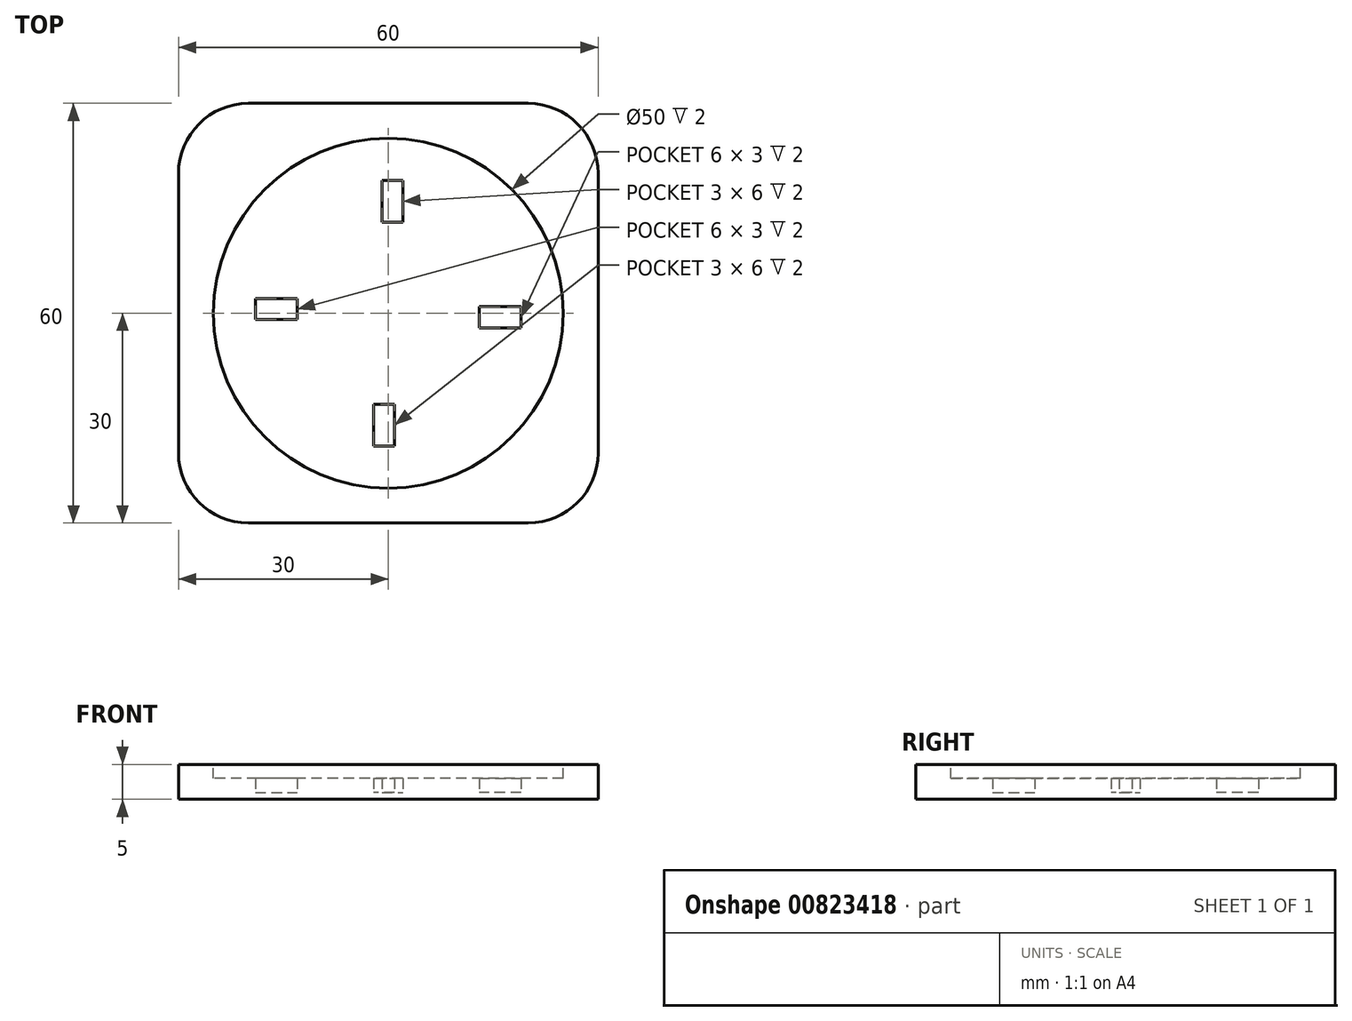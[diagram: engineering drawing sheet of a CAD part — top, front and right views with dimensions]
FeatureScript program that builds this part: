
annotation { "Feature Type Name" : "Feature", "Feature Type Description" : "" }
export const myFeature = defineFeature(function(context is Context, id is Id, definition is map)
    precondition{}
    {
        {
            var Q0;
            Q0=qCreatedBy(makeId("Top.planeOp"),FACE);
            var sketch = newSketch(context, id + "F0", { "sketchPlane" : qUnion([Q0])});
            skLineSegment(sketch, "E0.bottom", {"start": v(30, 30) * mm, "end": v(-30, 30) * mm});
            skLineSegment(sketch, "E0.top", {"start": v(30, -30) * mm, "end": v(-30, -30) * mm});
            skLineSegment(sketch, "E0.left", {"start": v(30, 30) * mm, "end": v(30, -30) * mm});
            skLineSegment(sketch, "E0.right", {"start": v(-30, 30) * mm, "end": v(-30, -30) * mm});
            skPoint(sketch, "E0.middle", {"position": v(0, 0) * mm});
            skSolve(sketch);
        }
        {
            var Q0;
            Q0 = qSketchRegion(id + "F0", true);
            extrude(context, id + "F1", {"entities" : qUnion([Q0]), "depth" : 5 * mm, "offsetDistance" : 25 * mm});
        }
        {
            var Q0;
            Q0=makeQuery(id+"F1.opExtrude","CAP_FACE",FACE,{"disambiguationData":[OSD([sQuery(id+"F0.wireOp",EDGE,"E0.bottom"),sQuery(id+"F0.wireOp",EDGE,"E0.top"),sQuery(id+"F0.wireOp",EDGE,"E0.left"),sQuery(id+"F0.wireOp",EDGE,"E0.right")])],"isStart":false});
            var sketch = newSketch(context, id + "F2", { "sketchPlane" : qUnion([Q0])});
            skCircle(sketch, "E1", {"center": v(0, 0) * mm, "radius": 25 * mm});
            skSolve(sketch);
        }
        {
            var Q0;
            Q0 = qSketchRegion(id + "F2", true);
            extrude(context, id + "F3", {"entities" : qUnion([Q0]), "operationType" : NewBodyOperationType.REMOVE, "oppositeDirection" : true, "depth" : 2 * mm, "offsetDistance" : 25 * mm});
        }
        {
            var Q0;
            Q0=makeQuery(id+"F3.boolean.opBoolean","COPY",FACE,{"derivedFrom":makeQuery(id+"F3.opExtrude","CAP_FACE",FACE,{"disambiguationData":[OSD([sQuery(id+"F2.wireOp",EDGE,"E1")])],"isStart":false})});
            var sketch = newSketch(context, id + "F4", { "sketchPlane" : qUnion([Q0])});
            skLineSegment(sketch, "E2.bottom", {"start": v(-0.91, 19) * mm, "end": v(2.09, 19) * mm});
            skLineSegment(sketch, "E2.top", {"start": v(-0.91, 13) * mm, "end": v(2.09, 13) * mm});
            skLineSegment(sketch, "E2.left", {"start": v(-0.91, 19) * mm, "end": v(-0.91, 13) * mm});
            skLineSegment(sketch, "E2.right", {"start": v(2.09, 19) * mm, "end": v(2.09, 13) * mm});
            skPoint(sketch, "E3.left.start.orphan", {"position": v(8.09, 0) * mm});
            skLineSegment(sketch, "E4.1.0", {"start": v(-19, 2.09) * mm, "end": v(-13, 2.09) * mm});
            skLineSegment(sketch, "E4.1.1", {"start": v(-19, -0.91) * mm, "end": v(-13, -0.91) * mm});
            skLineSegment(sketch, "E4.1.2", {"start": v(-19, -0.91) * mm, "end": v(-19, 2.09) * mm});
            skLineSegment(sketch, "E4.1.3", {"start": v(-13, -0.91) * mm, "end": v(-13, 2.09) * mm});
            skLineSegment(sketch, "E4.2.0", {"start": v(-2.09, -19) * mm, "end": v(-2.09, -13) * mm});
            skLineSegment(sketch, "E4.2.1", {"start": v(0.91, -19) * mm, "end": v(0.91, -13) * mm});
            skLineSegment(sketch, "E4.2.2", {"start": v(0.91, -19) * mm, "end": v(-2.09, -19) * mm});
            skLineSegment(sketch, "E4.2.3", {"start": v(0.91, -13) * mm, "end": v(-2.09, -13) * mm});
            skLineSegment(sketch, "E4.3.0", {"start": v(19, -2.09) * mm, "end": v(13, -2.09) * mm});
            skLineSegment(sketch, "E4.3.1", {"start": v(19, 0.91) * mm, "end": v(13, 0.91) * mm});
            skLineSegment(sketch, "E4.3.2", {"start": v(19, 0.91) * mm, "end": v(19, -2.09) * mm});
            skLineSegment(sketch, "E4.3.3", {"start": v(13, 0.91) * mm, "end": v(13, -2.09) * mm});
            skPoint(sketch, "E4.center", {"position": v(0, 0) * mm});
            skSolve(sketch);
        }
        {
            var Q0;
            Q0=makeQuery(id+"F4.imprint","IMPRINT",FACE,{"disambiguationData":[TD([[makeQuery(id+"F4.imprint","IMPRINT",EDGE,{"derivedFrom":sQuery(id+"F4.wireOp",EDGE,"E4.2.0")}),-1.0]])]});
            var Q1;
            Q1=makeQuery(id+"F4.imprint","IMPRINT",FACE,{"disambiguationData":[TD([[makeQuery(id+"F4.imprint","IMPRINT",EDGE,{"derivedFrom":sQuery(id+"F4.wireOp",EDGE,"E4.1.0")}),-1.0]])]});
            var Q2;
            Q2=makeQuery(id+"F4.imprint","IMPRINT",FACE,{"disambiguationData":[TD([[makeQuery(id+"F4.imprint","IMPRINT",EDGE,{"derivedFrom":sQuery(id+"F4.wireOp",EDGE,"E2.bottom")}),-1.0]])]});
            var Q3;
            Q3=makeQuery(id+"F4.imprint","IMPRINT",FACE,{"disambiguationData":[TD([[makeQuery(id+"F4.imprint","IMPRINT",EDGE,{"derivedFrom":sQuery(id+"F4.wireOp",EDGE,"E4.3.0")}),-1.0]])]});
            extrude(context, id + "F5", {"entities" : qUnion([Q0, Q1, Q2, Q3]), "operationType" : NewBodyOperationType.REMOVE, "depth" : 2 * mm, "offsetDistance" : 25 * mm, "hasSecondDirection" : true, "secondDirectionOppositeDirection" : true, "secondDirectionDepth" : 2 * mm});
        }
        {
            var Q0;
            Q0=makeQuery(id+"F1.opExtrude","SWEPT_EDGE",EDGE,{"disambiguationData":[OSD([sQuery(id+"F0.wireOp",EDGE,"E0.bottom"),sQuery(id+"F0.wireOp",EDGE,"E0.right")])]});
            var Q1;
            Q1=makeQuery(id+"F1.opExtrude","SWEPT_EDGE",EDGE,{"disambiguationData":[OSD([sQuery(id+"F0.wireOp",EDGE,"E0.top"),sQuery(id+"F0.wireOp",EDGE,"E0.right")])]});
            var Q2;
            Q2=makeQuery(id+"F1.opExtrude","SWEPT_EDGE",EDGE,{"disambiguationData":[OSD([sQuery(id+"F0.wireOp",EDGE,"E0.top"),sQuery(id+"F0.wireOp",EDGE,"E0.left")])]});
            var Q3;
            Q3=makeQuery(id+"F1.opExtrude","SWEPT_EDGE",EDGE,{"disambiguationData":[OSD([sQuery(id+"F0.wireOp",EDGE,"E0.bottom"),sQuery(id+"F0.wireOp",EDGE,"E0.left")])]});
            fillet(context, id + "F6", {"entities" : qUnion([Q0, Q1, Q2, Q3]), "radius" : 10 * mm, "tangentPropagation" : true, "allowEdgeOverflow" : false});
        }
    });
